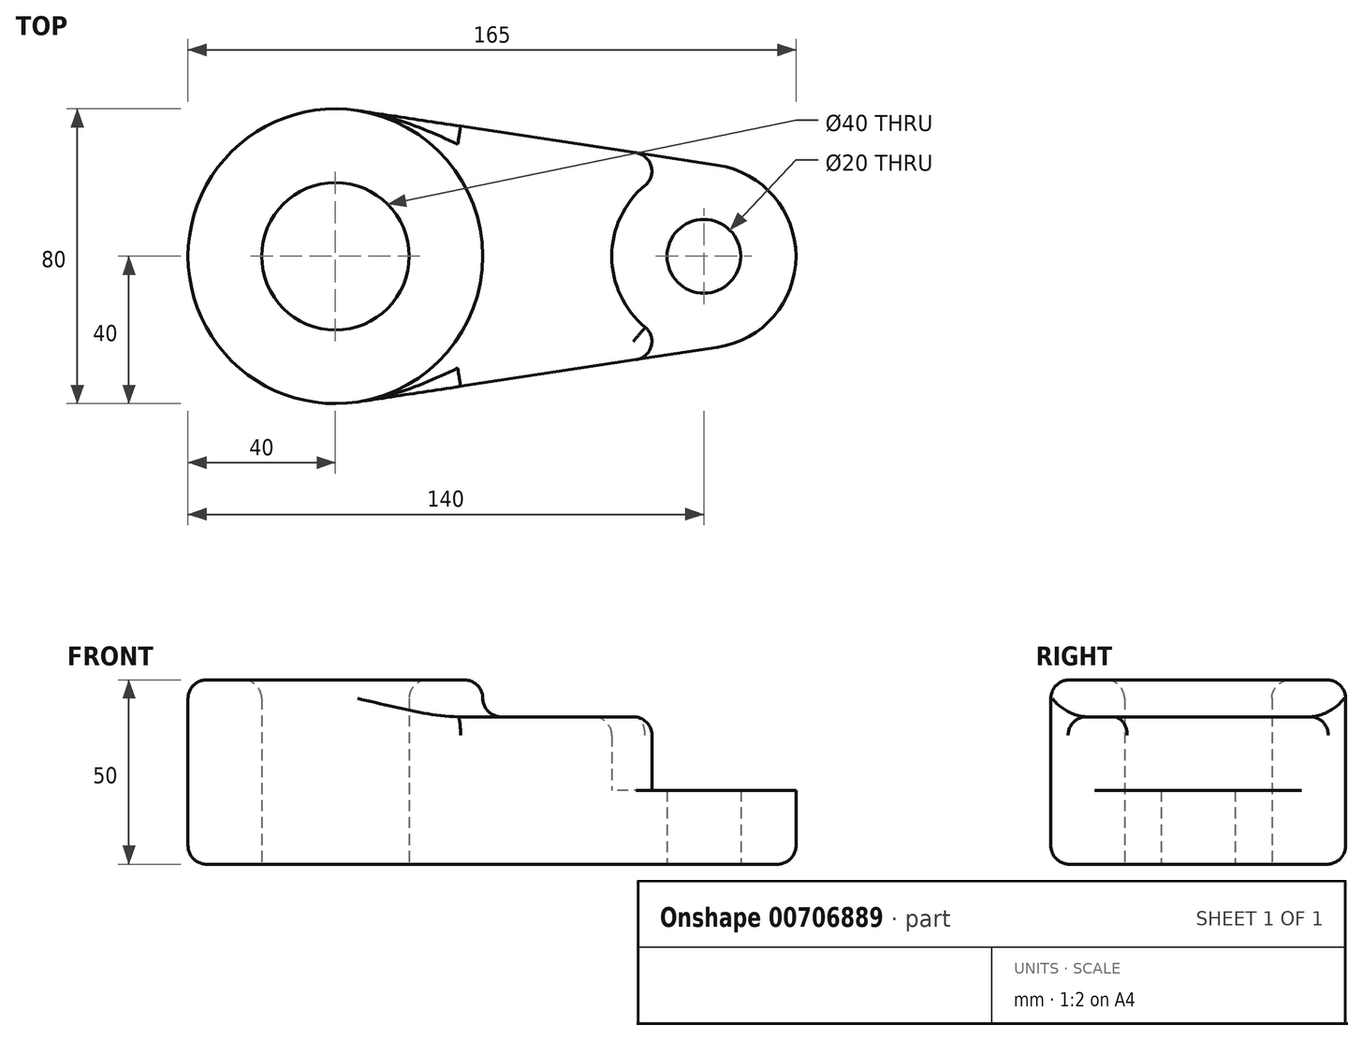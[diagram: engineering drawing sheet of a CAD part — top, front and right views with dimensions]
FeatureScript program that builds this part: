
annotation { "Feature Type Name" : "Feature", "Feature Type Description" : "" }
export const myFeature = defineFeature(function(context is Context, id is Id, definition is map)
    precondition{}
    {
        {
            var Q0;
            Q0=qCreatedBy(makeId("Top.planeOp"),FACE);
            var sketch = newSketch(context, id + "F0", { "sketchPlane" : qUnion([Q0])});
            skCircle(sketch, "E0", {"center": v(-50, 0) * mm, "radius": 40 * mm});
            skCircle(sketch, "E1", {"center": v(-50, 0) * mm, "radius": 20 * mm});
            skCircle(sketch, "E2", {"center": v(50, 0) * mm, "radius": 25 * mm});
            skLineSegment(sketch, "E3", {"start": v(-44, 39.55) * mm, "end": v(53.75, 24.72) * mm});
            skLineSegment(sketch, "E4", {"start": v(-44, -39.55) * mm, "end": v(53.75, -24.72) * mm});
            skCircle(sketch, "E5", {"center": v(50, 0) * mm, "radius": 10 * mm});
            skSolve(sketch);
        }
        {
            var Q0;
            Q0=makeQuery(id+"F0.imprint","IMPRINT",FACE,{"disambiguationData":[TD([[makeQuery(id+"F0.imprint","IMPRINT",EDGE,{"derivedFrom":sQuery(id+"F0.wireOp",EDGE,"E1")}),-1.0]])]});
            extrude(context, id + "F1", {"entities" : qUnion([Q0]), "depth" : 50 * mm, "offsetDistance" : 25 * mm});
        }
        {
            var Q0;
            {var subQ0=sQuery(id+"F0.wireOp",EDGE,"E3");Q0=makeQuery(id+"F0.imprint","IMPRINT",FACE,{"disambiguationData":[TD([[makeQuery(id+"F0.imprint","IMPRINT",EDGE,{"derivedFrom":subQ0}),-1.0]])]});}
            extrude(context, id + "F2", {"entities" : qUnion([Q0]), "operationType" : NewBodyOperationType.ADD, "depth" : 40 * mm, "offsetDistance" : 25 * mm});
        }
        {
            var Q0;
            Q0=makeQuery(id+"F0.imprint","IMPRINT",FACE,{"disambiguationData":[TD([[makeQuery(id+"F0.imprint","IMPRINT",EDGE,{"derivedFrom":sQuery(id+"F0.wireOp",EDGE,"E5")}),-1.0]])]});
            extrude(context, id + "F3", {"entities" : qUnion([Q0]), "operationType" : NewBodyOperationType.ADD, "depth" : 20 * mm, "offsetDistance" : 25 * mm});
        }
        {
            var Q0;
            Q0=makeQuery(id+"F1.opExtrude","SWEPT_FACE",FACE,{"disambiguationData":[OSD([sQuery(id+"F0.wireOp",EDGE,"E0")])]});
            var Q1;
            {var subQ0=sQuery(id+"F0.wireOp",EDGE,"E4");var subQ1=sQuery(id+"F0.wireOp",EDGE,"E2");Q1=makeQuery(id+"F3.boolean.opBoolean","SPLIT",EDGE,{"disambiguationData":[topologyDisambiguationEdgeConnected([makeQuery(id+"F2.opExtrude","SWEPT_FACE",FACE,{"disambiguationData":[OSD([subQ1])]})])],"derivedFrom":makeQuery(id+"F2.opExtrude","SWEPT_EDGE",EDGE,{"disambiguationData":[OSD([subQ0,subQ1])]})});}
            var Q2;
            {var subQ0=sQuery(id+"F0.wireOp",EDGE,"E3");var subQ1=sQuery(id+"F0.wireOp",EDGE,"E2");Q2=makeQuery(id+"F3.boolean.opBoolean","SPLIT",EDGE,{"disambiguationData":[topologyDisambiguationEdgeConnected([makeQuery(id+"F2.opExtrude","SWEPT_FACE",FACE,{"disambiguationData":[OSD([subQ1])]})])],"derivedFrom":makeQuery(id+"F2.opExtrude","SWEPT_EDGE",EDGE,{"disambiguationData":[OSD([subQ0,subQ1])]})});}
            fillet(context, id + "F4", {"entities" : qUnion([Q0, Q1, Q2]), "radius" : 5 * mm, "tangentPropagation" : true, "allowEdgeOverflow" : false});
        }
        {
            var Q0;
            Q0=makeQuery(id+"F2.opExtrude","CAP_EDGE",EDGE,{"disambiguationData":[OSD([sQuery(id+"F0.wireOp",EDGE,"E4")])],"isStart":false});
            var Q1;
            Q1=makeQuery(id+"F2.opExtrude","CAP_EDGE",EDGE,{"disambiguationData":[OSD([sQuery(id+"F0.wireOp",EDGE,"E3")])],"isStart":false});
            var Q2;
            Q2=makeQuery(id+"F1.opExtrude","CAP_EDGE",EDGE,{"disambiguationData":[OSD([sQuery(id+"F0.wireOp",EDGE,"E1")])],"isStart":false});
            var Q3;
            Q3=makeQuery(id+"F4.opFillet","BLEND_EDGE",EDGE,{"blendedFrom":[makeQuery(id+"F2.opExtrude","CAP_EDGE",EDGE,{"disambiguationData":[OSD([sQuery(id+"F0.wireOp",EDGE,"E0")])],"isStart":false}),makeQuery(id+"F2.opExtrude","SWEPT_FACE",FACE,{"disambiguationData":[OSD([sQuery(id+"F0.wireOp",EDGE,"E4")])]})],"blendedInto":[makeQuery(id+"F2.opExtrude","SWEPT_FACE",FACE,{"disambiguationData":[OSD([sQuery(id+"F0.wireOp",EDGE,"E4")])]})]});
            var Q4;
            Q4=makeQuery(id+"F4.opFillet","BLEND_EDGE",EDGE,{"blendedFrom":[makeQuery(id+"F2.opExtrude","CAP_EDGE",EDGE,{"disambiguationData":[OSD([sQuery(id+"F0.wireOp",EDGE,"E0")])],"isStart":false}),makeQuery(id+"F2.opExtrude","SWEPT_FACE",FACE,{"disambiguationData":[OSD([sQuery(id+"F0.wireOp",EDGE,"E3")])]})],"blendedInto":[makeQuery(id+"F2.opExtrude","SWEPT_FACE",FACE,{"disambiguationData":[OSD([sQuery(id+"F0.wireOp",EDGE,"E3")])]})]});
            fillet(context, id + "F5", {"entities" : qUnion([Q0, Q1, Q2, Q3, Q4]), "radius" : 5 * mm, "tangentPropagation" : true, "allowEdgeOverflow" : false});
        }
    });
